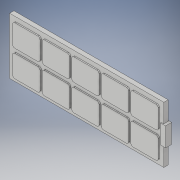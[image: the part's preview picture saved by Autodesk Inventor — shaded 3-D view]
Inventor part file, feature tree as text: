
AUTODESK INVENTOR PART (.ipt)
format: ipt  version: 2018 (Build 220112000, 112)  size: 233,984 bytes
history: native  units: in
note: dims shown in document units (in); Inventor stores cm internally (conversion verified against a paired STEP export)
features: extrude x3, sketch x3, plane x1
ambient origin geometry x8: Origin, YZ Plane, XZ Plane, XY Plane, X Axis, Y Axis, Z Axis, Center Point
bodies: Solid1 (feature_tree)
feature tree (7):
  extrude  "Extrusion1"  Depth=5.1181in
  extrude  "Extrusion2"  Depth=0.3937in
  plane  "Work Plane1"
  extrude  "Extrusion3"  Depth=2.0001in
  sketch  "Sketch1"  dims[d0=13.9764in d1=5.1181in]
  sketch  "Sketch2"  dims[d2=0.3937in d3=0.0in d4=0.3937in]
  sketch  "Sketch3"  dims[d5=0.3937in d7=2.0001in d8=2.4803in d9=0.1969in d10=1.9685in d12=2.6772in d13=0.3937in d15=0.3937in d17=0.7874in d19=2.3938in d20=0.3937in d22=0.3937in d24=0.4724in d25=1.7323in d28=0.1181in d29=0.0in d30=-0.1969in d31=0.4724in d32=1.7323in d33=0.5512in d34=0.0in]
